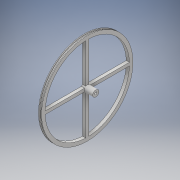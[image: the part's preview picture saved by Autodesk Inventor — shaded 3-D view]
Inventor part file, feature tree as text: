
AUTODESK INVENTOR PART (.ipt)
format: ipt  version: 2018 (Build 220112000, 112)  size: 329,728 bytes
history: native  units: mm
features: extrude x7, sketch x7, pattern_circular x1
ambient origin geometry x8: Origin, YZ Plane, XZ Plane, XY Plane, X Axis, Y Axis, Z Axis, Center Point
bodies: Solid1 (feature_tree)
feature tree (15):
  extrude  "Extrusion1"  Depth=2.0mm TaperAngle=0.0deg
  extrude  "Extrusion2"  Depth=1.0mm TaperAngle=0.0deg
  extrude  "Extrusion3"  Depth=1.0mm
  extrude  "Extrusion4"  Depth=3.0mm
  extrude  "Extrusion5"  Depth=5.0mm TaperAngle=0.0deg
  extrude  "Extrusion6"  Depth=4.0mm
  pattern_circular  "Circular Pattern1"  Count=4 Angle=360.0deg
  extrude  "Extrusion7"  Depth=15.0mm
  sketch  "Sketch1"  dims[d0=115.0mm d1=2.0mm d2=0.0mm]
  sketch  "Sketch2"  dims[d3=117.0mm d4=1.0mm d5=0.0mm]
  sketch  "Sketch3"  dims[d6=1.0mm d7=0.0mm d8=108.0mm]
  sketch  "Sketch4"  dims[d9=5.0mm d10=0.0mm d11=3.0mm]
  sketch  "Sketch5"  dims[d12=7.0mm d13=5.0mm d14=0.0mm]
  sketch  "Sketch6"  dims[d15=2.0mm d16=4.0mm]
  sketch  "Sketch7"  dims[d17=4.0mm d18=0.0mm d19=40.0mm d20=360.0deg d22=8.0mm d23=15.0mm d24=0.0mm]
